# Revit family: Skylight-Wasco-CS-Standard_Unit
name_source: partatom
category: Windows
revit_build: Autodesk Revit Architecture 2013 (Build: 20130531_2115(x64)
units: mm (PartAtom-declared; Revit-internal decimal feet)

## types (19) — shared parameters
Acrylic Glazing Inner = Acrylic - Wasco - Clear
Acrylic Glazing Outer = Acrylic - Wasco - Clear
Curb = Rubber, Black
Curb Height = 0' - 3 1/2"
Curb Width = 0' - 1 1/2"
Default Elevation = 0' - 0"
Description = Skylight
Finish = Aluminum - Wasco - Aged Copper
Host Constraint = 1
Manufacturer = Wasco
Overhang = 0' - 1 25/32"
Product Documentation Link = http://www.wascoskylights.com
Product Name = CS Standard Unit
Product Page URL = http://www.wascoskylights.com
URL = http://www.wascoskylights.com

## per-type parameters (varying)
| type | Height | Host Length | Host Width | L | Length | R | Rough Height | Rough Length | Rough Width | S | Width |
| DDCS2424 | 0' - 1 27/32" | 3' - 10" | 3' - 10" | 0' - 9 1/2" | 1' - 10" | 2' - 1 11/32" | 0' - 6 31/32" | 1' - 11 25/32" | 1' - 11 25/32" | 0' - 1 27/32" | 1' - 10" |
| DDCS2828 | 0' - 2 5/32" | 4' - 1 1/4" | 4' - 1 1/4" | 0' - 11 1/8" | 2' - 1 1/4" | 2' - 5 21/32" | 0' - 7 9/32" | 2' - 3 1/32" | 2' - 3 1/32" | 0' - 2 5/32" | 2' - 1 1/4" |
| DDCS2836 | 0' - 2 5/32" | 4' - 9 1/4" | 4' - 1 1/4" | 0' - 11 1/8" | 2' - 9 1/4" | 2' - 5 21/32" | 0' - 7 9/32" | 2' - 11 1/32" | 2' - 3 1/32" | 0' - 2 5/32" | 2' - 1 1/4" |
| DDCS2852 | 0' - 2 5/32" | 6' - 1 1/4" | 4' - 1 1/4" | 0' - 11 1/8" | 4' - 1 1/4" | 2' - 5 21/32" | 0' - 7 9/32" | 4' - 3 1/32" | 2' - 3 1/32" | 0' - 2 5/32" | 2' - 1 1/4" |
| DDCS3636 | 0' - 2 15/16" | 4' - 9 1/4" | 4' - 9 1/4" | 1' - 3 1/8" | 2' - 9 1/4" | 3' - 4 11/32" | 0' - 8 1/16" | 2' - 11 1/32" | 2' - 11 1/32" | 0' - 2 15/16" | 2' - 9 1/4" |
| DDCS3652 | 0' - 2 15/16" | 6' - 0 1/4" | 4' - 9 1/4" | 1' - 3 1/8" | 4' - 0 1/4" | 3' - 4 11/32" | 0' - 8 1/16" | 4' - 2 1/32" | 2' - 11 1/32" | 0' - 2 15/16" | 2' - 9 1/4" |
| DDCS3676 | 0' - 2 15/16" | 8' - 0 1/2" | 4' - 9 1/4" | 1' - 3 1/8" | 6' - 0 1/2" | 3' - 4 11/32" | 0' - 8 1/16" | 6' - 2 9/32" | 2' - 11 1/32" | 0' - 2 15/16" | 2' - 9 1/4" |
| DDCS4242 | 0' - 3 19/32" | 5' - 4" | 5' - 4" | 1' - 6 1/2" | 3' - 4" | 4' - 1 11/32" | 0' - 8 23/32" | 3' - 5 25/32" | 3' - 5 25/32" | 0' - 3 19/32" | 3' - 4" |
| DDCS4280 | 0' - 3 19/32" | 8' - 6" | 5' - 4" | 1' - 6 1/2" | 6' - 6" | 4' - 1 11/32" | 0' - 8 23/32" | 6' - 7 25/32" | 3' - 5 25/32" | 0' - 3 19/32" | 3' - 4" |
| DDCS5252 | 0' - 4 1/2" | 6' - 1 1/4" | 6' - 1 1/4" | 1' - 11 1/8" | 4' - 1 1/4" | 5' - 1 21/32" | 0' - 9 5/8" | 4' - 3 1/32" | 4' - 3 1/32" | 0' - 4 1/2" | 4' - 1 1/4" |
| DDCS5276 | 0' - 4 1/2" | 8' - 0 1/2" | 6' - 1 1/4" | 1' - 11 1/8" | 6' - 0 1/2" | 5' - 1 21/32" | 0' - 9 5/8" | 6' - 2 9/32" | 4' - 3 1/32" | 0' - 4 1/2" | 4' - 1 1/4" |
| DDCS5296 | 0' - 4 1/2" | 9' - 8 1/2" | 6' - 1 1/4" | 1' - 11 1/8" | 7' - 8 1/2" | 5' - 1 21/32" | 0' - 9 5/8" | 7' - 10 9/32" | 4' - 3 1/32" | 0' - 4 1/2" | 4' - 1 1/4" |
| DDCS6060 | 0' - 5 11/32" | 6' - 10" | 6' - 10" | 2' - 3 1/2" | 4' - 10" | 6' - 1 11/32" | 0' - 10 15/32" | 4' - 11 25/32" | 4' - 11 25/32" | 0' - 5 11/32" | 4' - 10" |
| DDCS6476 | 0' - 5 19/32" | 8' - 0 1/2" | 7' - 0 1/2" | 2' - 4 3/4" | 6' - 0 1/2" | 6' - 4 21/32" | 0' - 10 23/32" | 6' - 2 9/32" | 5' - 2 9/32" | 0' - 5 19/32" | 5' - 0 1/2" |
| DDCS6496 | 0' - 5 19/32" | 9' - 8 1/2" | 7' - 0 1/2" | 2' - 4 3/4" | 7' - 8 1/2" | 6' - 4 21/32" | 0' - 10 23/32" | 7' - 10 9/32" | 5' - 2 9/32" | 0' - 5 19/32" | 5' - 0 1/2" |
| DDCS7272 | 0' - 6 5/8" | 7' - 11" | 7' - 11" | 2' - 10" | 5' - 11" | 7' - 6 21/32" | 0' - 11 3/4" | 6' - 0 25/32" | 6' - 0 25/32" | 0' - 6 5/8" | 5' - 11" |
| DDCS8080 | 0' - 7 5/16" | 8' - 6" | 8' - 6" | 3' - 1 1/2" | 6' - 6" | 8' - 4" | 1' - 0 7/16" | 6' - 7 25/32" | 6' - 7 25/32" | 0' - 7 5/16" | 6' - 6" |
| DDCS9898 | 0' - 9" | 9' - 11 1/2" | 9' - 11 1/2" | 3' - 10 1/4" | 7' - 11 1/2" | 10' - 3 11/32" | 1' - 2 1/8" | 8' - 1 9/32" | 8' - 1 9/32" | 0' - 9" | 7' - 11 1/2" |
| Custom | 0' - 4 3/8" | 6' - 0" | 6' - 0" | 1' - 10 1/2" | 4' - 0" | 5' - 0" | 0' - 9 1/2" | 4' - 1 25/32" | 4' - 1 25/32" | 0' - 4 3/8" | 4' - 0" |

note: column(s) folded — value = type name in every type: Model

## geometry (parser evidence)
native form markers: Blend x22, Extrusion x1, Sweep x3
no freeform markers — native parametric forms only
